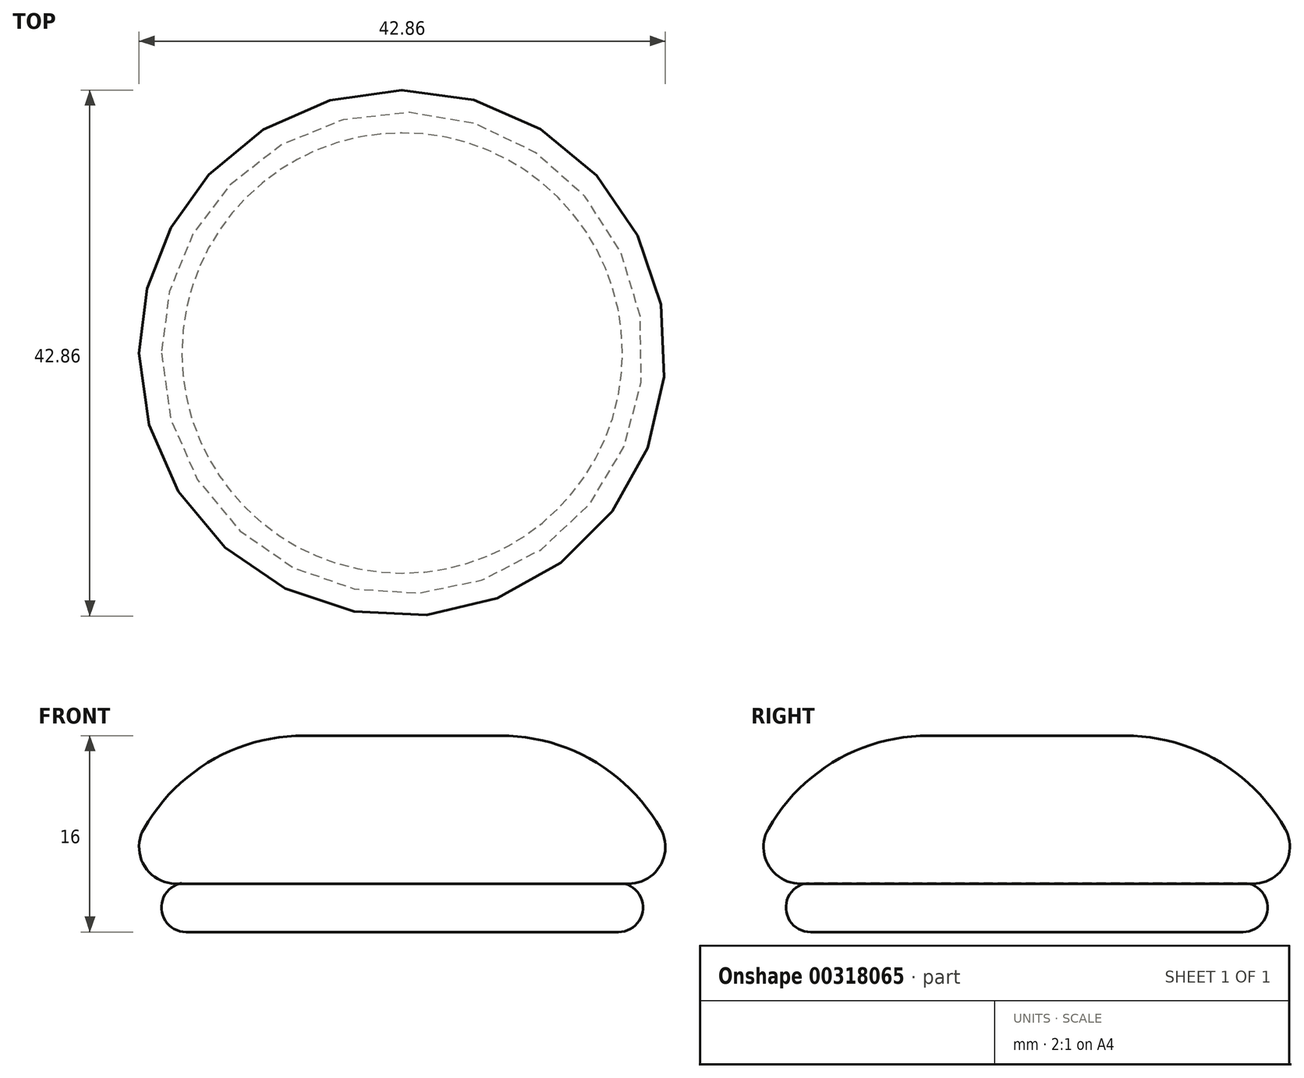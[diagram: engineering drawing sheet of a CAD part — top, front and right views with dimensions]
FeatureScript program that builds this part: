
annotation { "Feature Type Name" : "Feature", "Feature Type Description" : "" }
export const myFeature = defineFeature(function(context is Context, id is Id, definition is map)
    precondition{}
    {
        {
            var Q0;
            Q0=qCreatedBy(makeId("Front.planeOp"),FACE);
            var sketch = newSketch(context, id + "F0", { "sketchPlane" : qUnion([Q0])});
            skLineSegment(sketch, "E0", {"start": v(0, 0) * mm, "end": v(8, 0) * mm});
            skArc(sketch, "E1", {"start": v(21.04, -7.58) * mm, "mid": v(15.54, -2.03) * mm, "end": v(8, 0) * mm});
            skArc(sketch, "E2", {"start": v(17.94, -12.03) * mm, "mid": v(20.9, -10.78) * mm, "end": v(21.04, -7.58) * mm});
            skArc(sketch, "E3", {"start": v(17.61, -16) * mm, "mid": v(19.6, -14.16) * mm, "end": v(17.94, -12.03) * mm});
            skLineSegment(sketch, "E4", {"start": v(17.61, -16) * mm, "end": v(0, -16) * mm});
            skLineSegment(sketch, "E5", {"start": v(0, -16) * mm, "end": v(0, 0) * mm});
            skSolve(sketch);
        }
        {
            var Q0;
            Q0=makeQuery(id+"F0.imprint","IMPRINT",FACE,{"disambiguationData":[TD([[makeQuery(id+"F0.imprint","IMPRINT",EDGE,{"derivedFrom":sQuery(id+"F0.wireOp",EDGE,"E0")}),-1.0]])]});
            var Q1;
            Q1=sQuery(id+"F0.wireOp",EDGE,"E5");
            revolve(context, id + "F1", {"entities" : qUnion([Q0]), "axis" : qUnion([Q1]), "revolveType" : RevolveType.FULL});
        }
    });
